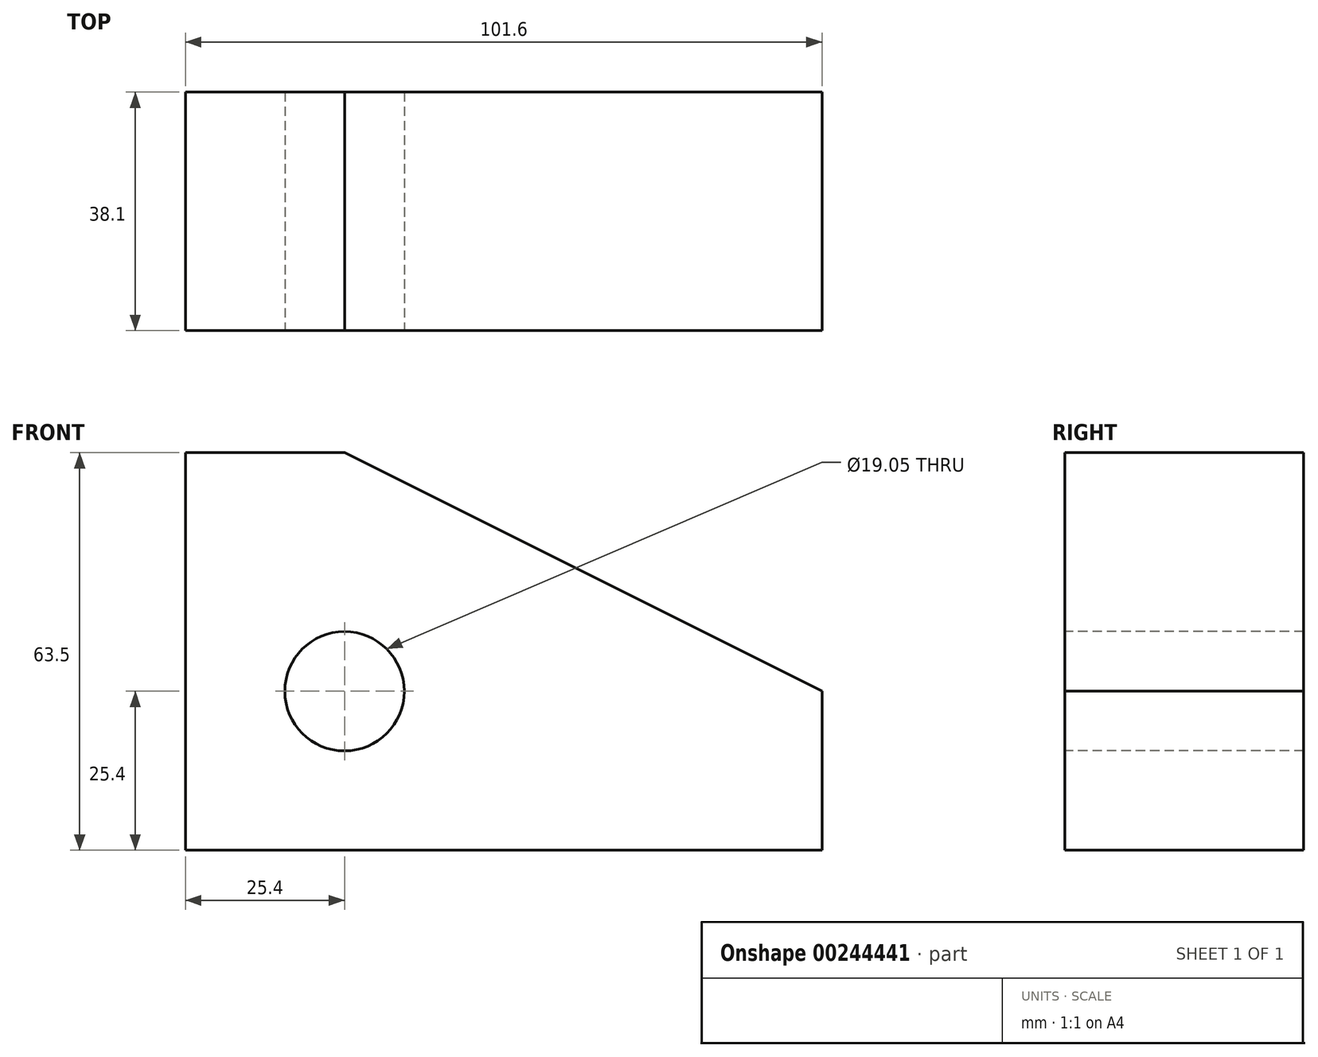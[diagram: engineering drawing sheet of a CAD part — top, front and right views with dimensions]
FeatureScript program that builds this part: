
annotation { "Feature Type Name" : "Feature", "Feature Type Description" : "" }
export const myFeature = defineFeature(function(context is Context, id is Id, definition is map)
    precondition{}
    {
        {
            var Q0;
            Q0=qCreatedBy(makeId("Front.planeOp"),FACE);
            var sketch = newSketch(context, id + "F0", { "sketchPlane" : qUnion([Q0])});
            skLineSegment(sketch, "E0", {"start": v(0, 0) * mm, "end": v(101.6, 0) * mm});
            skLineSegment(sketch, "E1", {"start": v(101.6, 0) * mm, "end": v(101.6, 25.4) * mm});
            skLineSegment(sketch, "E2", {"start": v(101.6, 25.4) * mm, "end": v(25.4, 63.5) * mm});
            skLineSegment(sketch, "E3", {"start": v(25.4, 63.5) * mm, "end": v(0, 63.5) * mm});
            skLineSegment(sketch, "E4", {"start": v(0, 63.5) * mm, "end": v(0, 0) * mm});
            skSolve(sketch);
        }
        {
            var Q0;
            Q0=makeQuery(id+"F0.imprint","IMPRINT",FACE,{"disambiguationData":[TD([[makeQuery(id+"F0.imprint","IMPRINT",EDGE,{"derivedFrom":sQuery(id+"F0.wireOp",EDGE,"E0")}),1.0]])]});
            extrude(context, id + "F1", {"entities" : qUnion([Q0]), "depth" : 38.1 * mm});
        }
        {
            var Q0;
            Q0=makeQuery(id+"F1.opExtrude","CAP_FACE",FACE,{"disambiguationData":[OSD([sQuery(id+"F0.wireOp",EDGE,"E0"),sQuery(id+"F0.wireOp",EDGE,"E1"),sQuery(id+"F0.wireOp",EDGE,"E2"),sQuery(id+"F0.wireOp",EDGE,"E3"),sQuery(id+"F0.wireOp",EDGE,"E4")])],"isStart":false});
            var sketch = newSketch(context, id + "F2", { "sketchPlane" : qUnion([Q0])});
            skCircle(sketch, "E5", {"center": v(25.4, 25.4) * mm, "radius": 9.53 * mm});
            skSolve(sketch);
        }
        {
            var Q0;
            Q0 = qSketchRegion(id + "F2", true);
            extrude(context, id + "F3", {"entities" : qUnion([Q0]), "operationType" : NewBodyOperationType.REMOVE, "endBound" : BoundingType.THROUGH_ALL, "oppositeDirection" : true, "depth" : 25.4 * mm});
        }
    });
